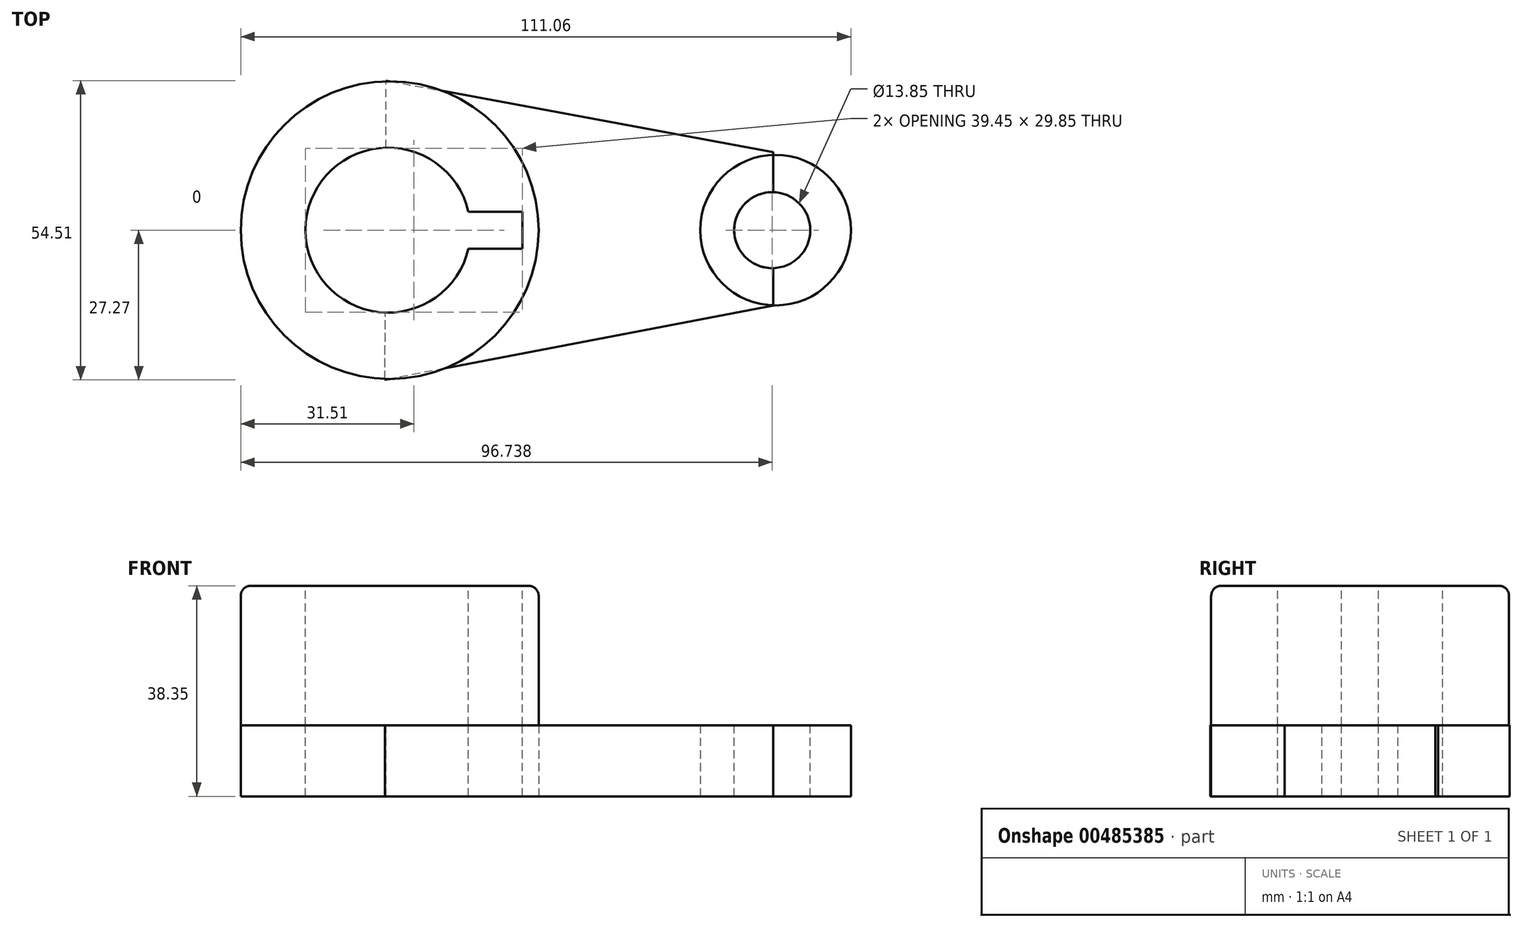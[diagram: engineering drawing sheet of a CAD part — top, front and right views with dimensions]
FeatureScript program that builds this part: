
annotation { "Feature Type Name" : "Feature", "Feature Type Description" : "" }
export const myFeature = defineFeature(function(context is Context, id is Id, definition is map)
    precondition{}
    {
        {
            var Q0;
            Q0=qCreatedBy(makeId("Top.planeOp"),FACE);
            var sketch = newSketch(context, id + "F0", { "sketchPlane" : qUnion([Q0])});
            skCircle(sketch, "E0", {"center": v(-47.03, 0) * mm, "radius": 27.1 * mm});
            skSolve(sketch);
        }
        {
            var Q0;
            Q0=qCreatedBy(makeId("Top.planeOp"),FACE);
            var sketch = newSketch(context, id + "F1", { "sketchPlane" : qUnion([Q0])});
            skCircle(sketch, "E1", {"center": v(23.2, 0) * mm, "radius": 13.72 * mm});
            skSolve(sketch);
        }
        {
            var Q0;
            Q0=qCreatedBy(makeId("Top.planeOp"),FACE);
            var sketch = newSketch(context, id + "F2", { "sketchPlane" : qUnion([Q0])});
            skLineSegment(sketch, "E2", {"start": v(-47.68, 0) * mm, "end": v(-47.68, 27.24) * mm});
            skLineSegment(sketch, "E3", {"start": v(-47.68, 27.24) * mm, "end": v(22.8, 14.23) * mm});
            skLineSegment(sketch, "E4", {"start": v(22.8, 14.23) * mm, "end": v(22.8, 0) * mm});
            skLineSegment(sketch, "E5", {"start": v(22.8, 0) * mm, "end": v(22.8, -13.76) * mm});
            skLineSegment(sketch, "E6", {"start": v(22.8, -13.76) * mm, "end": v(-47.93, -27.27) * mm});
            skLineSegment(sketch, "E7", {"start": v(-47.93, -27.27) * mm, "end": v(-47.68, 0) * mm});
            skSolve(sketch);
        }
        {
            var Q0;
            Q0=makeQuery(id+"F2.imprint","IMPRINT",FACE,{"disambiguationData":[TD([[makeQuery(id+"F2.imprint","IMPRINT",EDGE,{"derivedFrom":sQuery(id+"F2.wireOp",EDGE,"E2")}),-1.0]])]});
            var Q1;
            Q1=makeQuery(id+"F1.imprint","IMPRINT",FACE,{"disambiguationData":[TD([[makeQuery(id+"F1.imprint","IMPRINT",EDGE,{"derivedFrom":sQuery(id+"F1.wireOp",EDGE,"E1")}),1.0]])]});
            var Q2;
            Q2=makeQuery(id+"F0.imprint","IMPRINT",FACE,{"disambiguationData":[TD([[makeQuery(id+"F0.imprint","IMPRINT",EDGE,{"derivedFrom":sQuery(id+"F0.wireOp",EDGE,"E0")}),1.0]])]});
            extrude(context, id + "F3", {"entities" : qUnion([Q0, Q1, Q2]), "depth" : 12.95 * mm});
        }
        {
            var Q0;
            Q0=makeQuery(id+"F3.opExtrude","CAP_FACE",FACE,{"disambiguationData":[OSD([sQuery(id+"F0.wireOp",EDGE,"E0")])],"isStart":false});
            extrude(context, id + "F4", {"entities" : qUnion([Q0]), "depth" : 25.4 * mm});
        }
        {
            var Q0;
            Q0=qCreatedBy(makeId("Top.planeOp"),FACE);
            cPlane(context, id + "F5", {"entities" : qUnion([Q0]), "cplaneType" : CPlaneType.OFFSET, "offset" : 48.5 * mm, "width" : 152.4 * mm, "height" : 152.4 * mm});
        }
        {
            var Q0;
            Q0=qCreatedBy(id+"F5.planeOp",FACE);
            var sketch = newSketch(context, id + "F6", { "sketchPlane" : qUnion([Q0])});
            skCircle(sketch, "E8", {"center": v(-47.33, 0) * mm, "radius": 15.02 * mm});
            skSolve(sketch);
        }
        {
            var Q0;
            Q0=qCreatedBy(id+"F5.planeOp",FACE);
            var sketch = newSketch(context, id + "F7", { "sketchPlane" : qUnion([Q0])});
            skLineSegment(sketch, "E9.bottom", {"start": v(-39.4, 3.36) * mm, "end": v(-22.9, 3.36) * mm});
            skLineSegment(sketch, "E9.top", {"start": v(-39.4, -3.36) * mm, "end": v(-22.9, -3.36) * mm});
            skLineSegment(sketch, "E9.left", {"start": v(-39.4, 3.36) * mm, "end": v(-39.4, -3.36) * mm});
            skLineSegment(sketch, "E9.right", {"start": v(-22.9, 3.36) * mm, "end": v(-22.9, -3.36) * mm});
            skSolve(sketch);
        }
        {
            var Q0;
            Q0 = qSketchRegion(id + "F6", true);
            var Q1;
            Q1 = qSketchRegion(id + "F7", true);
            extrude(context, id + "F8", {"entities" : qUnion([Q0, Q1]), "operationType" : NewBodyOperationType.REMOVE, "oppositeDirection" : true, "depth" : 56.13 * mm});
        }
        {
            var Q0;
            Q0=makeQuery(id+"F4.opExtrude","CAP_EDGE",EDGE,{"disambiguationData":[OSD([sQuery(id+"F0.wireOp",EDGE,"E0")])],"isStart":false});
            fillet(context, id + "F9", {"entities" : qUnion([Q0]), "radius" : 1.84 * mm, "tangentPropagation" : true, "allowEdgeOverflow" : false});
        }
        {
            var Q0;
            Q0=qCreatedBy(makeId("Top.planeOp"),FACE);
            cPlane(context, id + "F10", {"entities" : qUnion([Q0]), "cplaneType" : CPlaneType.OFFSET, "offset" : 16 * mm, "width" : 152.4 * mm, "height" : 152.4 * mm});
        }
        {
            var Q0;
            Q0=qCreatedBy(id+"F10.planeOp",FACE);
            var sketch = newSketch(context, id + "F11", { "sketchPlane" : qUnion([Q0])});
            skCircle(sketch, "E10", {"center": v(22.6, 0) * mm, "radius": 6.92 * mm});
            skSolve(sketch);
        }
        {
            var Q0;
            Q0 = qSketchRegion(id + "F11", true);
            extrude(context, id + "F12", {"entities" : qUnion([Q0]), "operationType" : NewBodyOperationType.REMOVE, "oppositeDirection" : true, "depth" : 40.9 * mm});
        }
    });
